# Revit family: Shower-Valve_Trim-KOHLER-MODULO-K-76690T
name_source: partatom
category: Plumbing Fixtures
revit_build: Autodesk Revit 2017 (Build: 20160225_1515(x64)
units: mm (PartAtom-declared; Revit-internal decimal feet)

## family parameters
Cut with Voids When Loaded = No
Host = Face
OmniClass Number = 23.31.25.00
OmniClass Title = Toilet and Bath Specialties
Part Type = Normal
Room Calculation Point = No
Round Connector Dimension = Use Diameter
Shared = No

## types (2) — shared parameters
ADA Compliant = No
Assembly Code = D2010700
CW Connection = Yes
Cold Water Inlet = Cold Water Inlet
Date Modified = 6/25/2020
Default Elevation = 42"
Description = Smart matching wall-mounted thermostatic bathtub shower valve core and panel Ai Fei handle
Drain Included = No
Flow Rate = 0 GPM
HW Connection = Yes
Height = 7 1/16"
Hot Water Inlet = Hot Water Inlet
Length = 3 5/16"
Manufacturer = KOHLER Co.
Master Format 2014 = 22.42.23
Master Format 2014 Name = Residential Showers
Material = Premium Metal Construction
Pressure = 72.52 psi
Product Documentation Link = http://files.kohler.com.cn
Product Name = MODULO
Product Page URL = http://www.kohler.com.cn
Tempered Water Outlet 1 = Tempered Water Outlet 1
Tempered Water Outlet 2 = Tempered Water Outlet 2
URL = http://www.kohler.com.cn
Vent Connection = No
Waste Connection = No
Waste Water Outlet = Waste Water Outlet
WaterSense Certified = No
Width = 7 1/16"

## per-type parameters (varying)
| type | Finish | Model | Type |
| CP-Polished Chrome | Kohler-Metal-CP-Polished_Chrome | K-76690T-9-CP | 1 |
| TT-Titanium Silver | Kohler-Metal-TT-Titanium_Silver | K-76690T-9-TT | 2 |

## geometry (parser evidence)
native form markers: Sweep x4
no freeform markers — native parametric forms only
